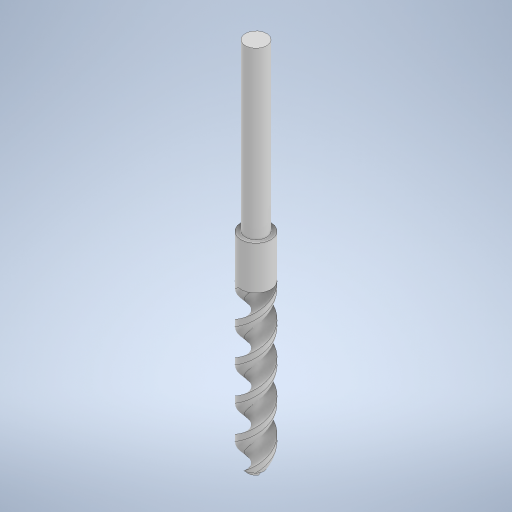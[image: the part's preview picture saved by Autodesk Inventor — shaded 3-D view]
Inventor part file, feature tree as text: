
AUTODESK INVENTOR PART (.ipt)
format: ipt  version: 2024.2 (Build 282272000, 272)  size: 634,368 bytes
history: native  units: mm
features: sketch x5, extrude x3, helix x1, pattern_circular x1, revolve x1, fillet x1
ambient origin geometry x8: Origin, YZ Plane, XZ Plane, XY Plane, X Axis, Y Axis, Z Axis, Center Point
bodies: Body1 (feature_tree)
feature tree (12):
  extrude  "Extrusion3"  Depth=60.0mm TaperAngle=0.0deg
  extrude  "Extrusion4"  Depth=3.0mm TaperAngle=0.0deg
  helix  "Coil2"  [1 undecoded]
  pattern_circular  "Circular Pattern2"  Count=2 Angle=360.0deg
  revolve  "Revolution1"  Angle=90.0deg
  fillet  "Fillet5"  Radius=1.7638mm
  extrude  "Extrusion5"  Depth=50.0mm TaperAngle=0.0deg
  sketch  "Sketch9"  dims[d25=9.0mm d26=60.0mm d27=0.0mm]
  sketch  "Sketch10"  dims[d28=5.0mm d29=3.0mm d30=0.0mm d32=7.0mm]
  sketch  "Sketch12"  dims[d33=20.0mm d34=50.0mm d35=10.0mm d36=0.0mm d37=90.0deg d38=90.0deg d39=0.0mm d40=0.0mm d41=20.0mm d42=360.0deg]
  sketch  "Sketch16"  dims[d45=1.0mm d46=90.0deg d47=1.7638mm]
  sketch  "Sketch18"  dims[d48=6.44mm d49=50.0mm d50=0.0mm d1=0.5mm d2=0.872665mm d3=0.5mm d4=0.872665mm d44=0.0mm]
note: 1 required parameter value undecoded (feature->parameter linkage not recoverable at this tier; creation-order binding heuristic only, values carry confidence <= 0.55)
